# Revit family: KEUCO_14953010100
name_source: partatom
category: Sonderausstattung
revit_build: Autodesk Revit 2016 (Build: 20150220_1215(x64)
units: mm (PartAtom-declared; Revit-internal decimal feet)

## family parameters
Arbeitsebenenbasiert = Nein
Beim Laden mit Abzugskörper schneiden = Nein
Bemaßung runder Anschluss = Durchmesser verwenden
Gemeinsam genutzt = Nein
Immer vertikal = Ja
Raumberechnungspunkt = Nein
Teiletyp = Normal

## types (3) — shared parameters
Beschreibung = Wandmodell, komplett mit Halter,
Kunststoffeinsatz und Pumpe
Füllmenge: ca. 250 ml
Dosiermenge: ca. 0,5 ml/Hub
Gewicht = 382
Hersteller = KEUCO
Kategorie = ACC
Preisgruppe = 1
Serie = Plan
URL = https://www.keuco.com
Verwendung = BI / GWC / WP

## per-type parameters (varying)
| type | Ausschreibungstext |
| 14953010100 | KEUCO PLAN Lotionspender 14953010100 
Hochglanzverchromter Lotionspender, Wandmodell 
in ästhetischem, funktionalem Design
komplett mit herausnehmbarem Kunststoffeinsatz 
für leichtes Reinigen und leichtes Befüllen
hochwertige und langlebige Pumpe
Füllmenge ca. 250 ml, für handelsübliche Flüssigseifen
Dosiermenge ca. 0,5 ml/Hub
Grundkörperdurchmesser 65 mm, Höhe 179 mm, Ausladung 123 mm
Der Lotionspender wird verdeckt angebracht
Lieferung inkl. korrosionsfreiem Befestigungsmaterial |
| 14953070100 | KEUCO PLAN Lotionspender 14953070100 
Lotionspender aus hochwertigem Edelstahl, Wandmodell
in ästhetischem, funktionalem Design
komplett mit herausnehmbarem Kunststoffeinsatz 
für leichtes Reinigen und leichtes Befüllen
hochwertige und langlebige Pumpe
Füllmenge ca. 250 ml, für handelsübliche Flüssigseifen
Dosiermenge ca. 0,5 ml/Hub
Grundkörperdurchmesser 65 mm, Höhe 179 mm, Ausladung 123 mm
Der Lotionspender wird verdeckt angebracht
Lieferung inkl. korrosionsfreiem Befestigungsmaterial |
| 14953170100 | KEUCO PLAN Lotionspender 14953170100 
Lotionspender aus silber-eloxiertem Aluminium (E6 EV1)/verchromt 
in ästhetischem, funktionalem Design
Wandmodell, komplett mit herausnehmbarem Kunststoffeinsatz 
für leichtes Reinigen und leichtes Befüllen
hochwertige und langlebige Pumpe
Die Wandhalterung ist als Design-Element hochglanzverchromt
Füllmenge ca. 250 ml, für handelsübliche Flüssigseifen
Dosiermenge ca. 0,5 ml/Hub
Grundkörperdurchmesser 65 mm, Höhe 179 mm, Ausladung 123 mm
Der Lotionspender wird verdeckt angebracht
Lieferung inkl. korrosionsfreiem Befestigungsmaterial |

note: column(s) folded — value = type name in every type: Artikelnummer

## geometry (parser evidence)
native form markers: Blend x2, Sweep x3
no freeform markers — native parametric forms only
